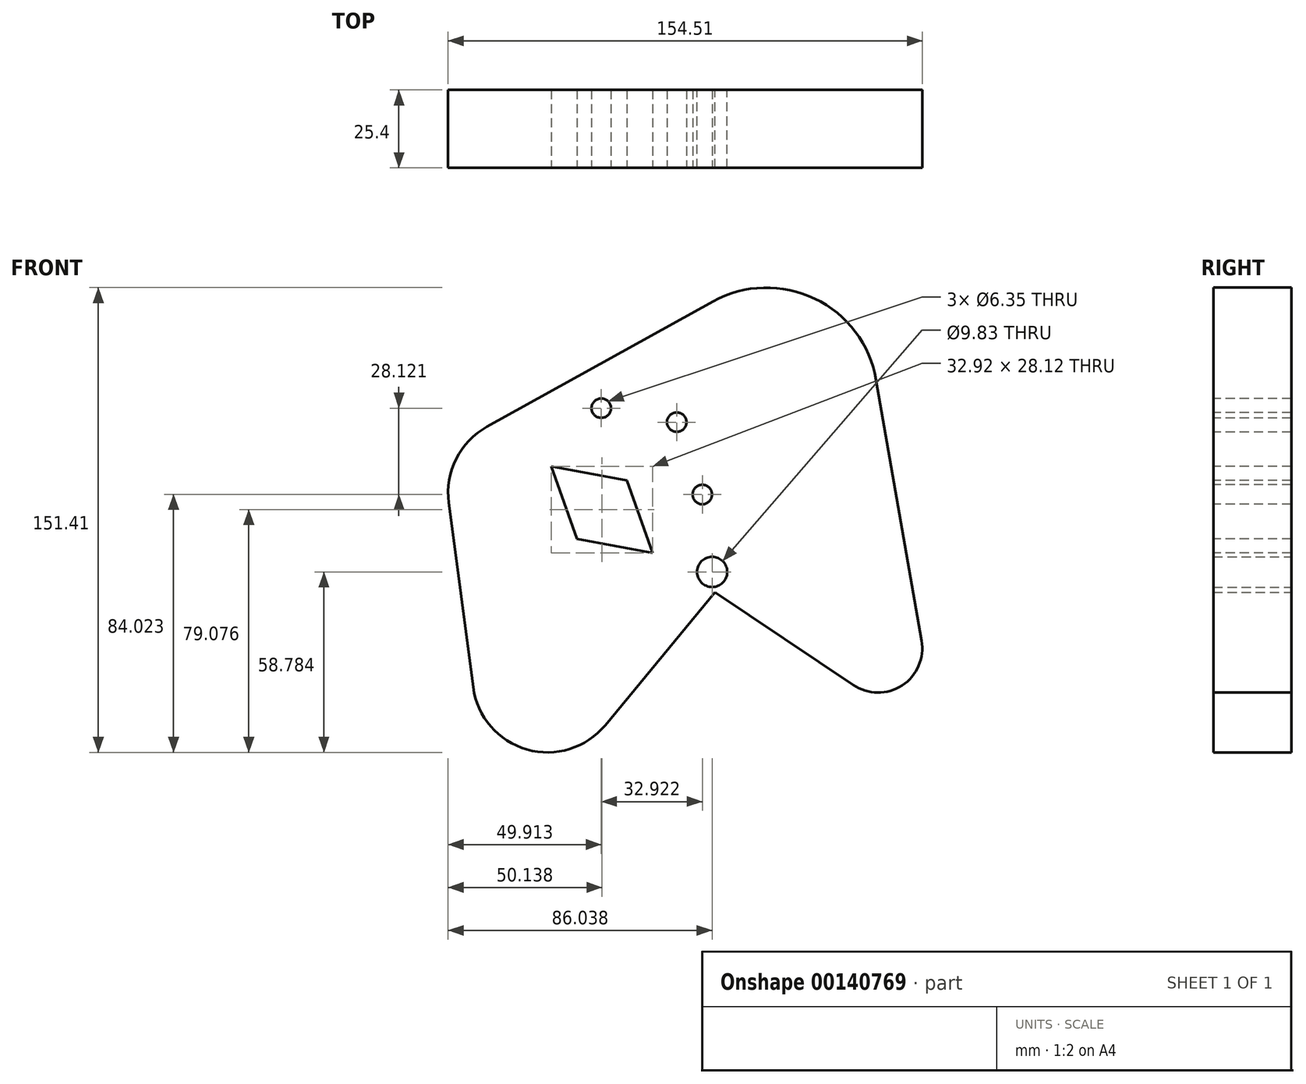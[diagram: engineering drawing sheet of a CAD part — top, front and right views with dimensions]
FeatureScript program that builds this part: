
annotation { "Feature Type Name" : "Feature", "Feature Type Description" : "" }
export const myFeature = defineFeature(function(context is Context, id is Id, definition is map)
    precondition{}
    {
        {
            var Q0;
            Q0=qCreatedBy(makeId("Front.planeOp"),FACE);
            var sketch = newSketch(context, id + "F0", { "sketchPlane" : qUnion([Q0])});
            skCircle(sketch, "E0", {"center": v(-69.46, 62.23) * mm, "radius": 24.64 * mm});
            skCircle(sketch, "E1", {"center": v(-61.73, 2.12) * mm, "radius": 24.43 * mm});
            skCircle(sketch, "E2", {"center": v(-8.07, 36.46) * mm, "radius": 4.92 * mm});
            skCircle(sketch, "E3", {"center": v(9.73, 92.97) * mm, "radius": 36.12 * mm});
            skCircle(sketch, "E4", {"center": v(45.96, 11.61) * mm, "radius": 14.43 * mm});
            skLineSegment(sketch, "E5", {"start": v(-81.4, 83.79) * mm, "end": v(-7.77, 124.57) * mm});
            skLineSegment(sketch, "E6", {"start": v(45.3, 99.33) * mm, "end": v(60.18, 14.1) * mm});
            skLineSegment(sketch, "E7", {"start": v(37.9, -0.37) * mm, "end": v(-10.81, 32.38) * mm});
            skLineSegment(sketch, "E8", {"start": v(-4.28, 33.34) * mm, "end": v(-44.43, -15.3) * mm});
            skLineSegment(sketch, "E9", {"start": v(-93.9, 59) * mm, "end": v(-85.95, -1.08) * mm});
            skSolve(sketch);
        }
        {
            var Q0;
            Q0 = qSketchRegion(id + "F0", true);
            extrude(context, id + "F1", {"entities" : qUnion([Q0]), "depth" : 25.4 * mm});
        }
        {
            var Q0;
            Q0=makeQuery(id+"F1.opExtrude","CAP_FACE",FACE,{"disambiguationData":[OSD([sQuery(id+"F0.wireOp",EDGE,"E0"),sQuery(id+"F0.wireOp",EDGE,"E1"),sQuery(id+"F0.wireOp",EDGE,"E2"),sQuery(id+"F0.wireOp",EDGE,"E3"),sQuery(id+"F0.wireOp",EDGE,"E4"),sQuery(id+"F0.wireOp",EDGE,"E5"),sQuery(id+"F0.wireOp",EDGE,"E6"),sQuery(id+"F0.wireOp",EDGE,"E7"),sQuery(id+"F0.wireOp",EDGE,"E8"),sQuery(id+"F0.wireOp",EDGE,"E9")])],"isStart":false});
            var sketch = newSketch(context, id + "F2", { "sketchPlane" : qUnion([Q0])});
            skCircle(sketch, "E10.cCircle", {"center": v(-35.85, 66.26) * mm, "radius": 25 * mm, "construction": true});
            skLineSegment(sketch, "E10.0", {"start": v(-19.62, 85.27) * mm, "end": v(-11.28, 61.7) * mm});
            skLineSegment(sketch, "E10.1", {"start": v(-11.28, 61.7) * mm, "end": v(-27.51, 42.7) * mm});
            skLineSegment(sketch, "E10.2", {"start": v(-27.51, 42.7) * mm, "end": v(-52.09, 47.25) * mm});
            skLineSegment(sketch, "E10.3", {"start": v(-52.09, 47.25) * mm, "end": v(-60.43, 70.82) * mm});
            skLineSegment(sketch, "E10.4", {"start": v(-60.43, 70.82) * mm, "end": v(-44.2, 89.82) * mm});
            skLineSegment(sketch, "E10.5", {"start": v(-44.2, 89.82) * mm, "end": v(-19.62, 85.27) * mm});
            skLineSegment(sketch, "E11", {"start": v(-60.43, 70.82) * mm, "end": v(-11.28, 61.7) * mm});
            skLineSegment(sketch, "E12", {"start": v(-52.09, 47.25) * mm, "end": v(-19.62, 85.27) * mm});
            skLineSegment(sketch, "E13", {"start": v(-44.2, 89.82) * mm, "end": v(-27.51, 42.7) * mm});
            skSolve(sketch);
        }
        {
            var Q0;
            {var subQ0=sQuery(id+"F2.wireOp",EDGE,"E10.3");Q0=makeQuery(id+"F2.imprint","IMPRINT",FACE,{"disambiguationData":[TD([[makeQuery(id+"F2.imprint","IMPRINT",EDGE,{"derivedFrom":subQ0}),-1.0]])]});}
            extrude(context, id + "F3", {"entities" : qUnion([Q0]), "operationType" : NewBodyOperationType.REMOVE, "oppositeDirection" : true, "depth" : 25.4 * mm});
        }
        {
            var Q0;
            {var subQ0=sQuery(id+"F2.wireOp",EDGE,"E10.2");Q0=makeQuery(id+"F2.imprint","IMPRINT",FACE,{"disambiguationData":[TD([[makeQuery(id+"F2.imprint","IMPRINT",EDGE,{"derivedFrom":subQ0}),-1.0]])]});}
            extrude(context, id + "F4", {"entities" : qUnion([Q0]), "operationType" : NewBodyOperationType.REMOVE, "oppositeDirection" : true, "depth" : 25.4 * mm});
        }
        {
            var Q0;
            Q0=sQuery(id+"F2.wireOp",VERTEX,"E12.end");
            var Q1;
            Q1=makeQuery(id+"F1.opExtrude","SWEPT_BODY",BODY,{"disambiguationData":[OSD([sQuery(id+"F0.wireOp",EDGE,"E0"),sQuery(id+"F0.wireOp",EDGE,"E1"),sQuery(id+"F0.wireOp",EDGE,"E2"),sQuery(id+"F0.wireOp",EDGE,"E3"),sQuery(id+"F0.wireOp",EDGE,"E4"),sQuery(id+"F0.wireOp",EDGE,"E5"),sQuery(id+"F0.wireOp",EDGE,"E6"),sQuery(id+"F0.wireOp",EDGE,"E7"),sQuery(id+"F0.wireOp",EDGE,"E8"),sQuery(id+"F0.wireOp",EDGE,"E9")])]});
            hole(context, id + "F5", {"style" : HoleStyle.SIMPLE, "endStyle" : HoleEndStyle.THROUGH, "holeDiameter" : 6.35 * mm, "locations" : qUnion([Q0]), "scope" : qUnion([Q1]), "isTappedThrough" : true});
        }
        {
            var Q0;
            Q0=sQuery(id+"F2.wireOp",VERTEX,"E13.start");
            var Q1;
            Q1=makeQuery(id+"F1.opExtrude","SWEPT_BODY",BODY,{"disambiguationData":[OSD([sQuery(id+"F0.wireOp",EDGE,"E0"),sQuery(id+"F0.wireOp",EDGE,"E1"),sQuery(id+"F0.wireOp",EDGE,"E2"),sQuery(id+"F0.wireOp",EDGE,"E3"),sQuery(id+"F0.wireOp",EDGE,"E4"),sQuery(id+"F0.wireOp",EDGE,"E5"),sQuery(id+"F0.wireOp",EDGE,"E6"),sQuery(id+"F0.wireOp",EDGE,"E7"),sQuery(id+"F0.wireOp",EDGE,"E8"),sQuery(id+"F0.wireOp",EDGE,"E9")])]});
            hole(context, id + "F6", {"style" : HoleStyle.SIMPLE, "endStyle" : HoleEndStyle.THROUGH, "holeDiameter" : 6.35 * mm, "locations" : qUnion([Q0]), "scope" : qUnion([Q1]), "isTappedThrough" : true});
        }
        {
            var Q0;
            Q0=sQuery(id+"F2.wireOp",VERTEX,"E10.1.start");
            var Q1;
            Q1=makeQuery(id+"F1.opExtrude","SWEPT_BODY",BODY,{"disambiguationData":[OSD([sQuery(id+"F0.wireOp",EDGE,"E0"),sQuery(id+"F0.wireOp",EDGE,"E1"),sQuery(id+"F0.wireOp",EDGE,"E2"),sQuery(id+"F0.wireOp",EDGE,"E3"),sQuery(id+"F0.wireOp",EDGE,"E4"),sQuery(id+"F0.wireOp",EDGE,"E5"),sQuery(id+"F0.wireOp",EDGE,"E6"),sQuery(id+"F0.wireOp",EDGE,"E7"),sQuery(id+"F0.wireOp",EDGE,"E8"),sQuery(id+"F0.wireOp",EDGE,"E9")])]});
            hole(context, id + "F7", {"style" : HoleStyle.SIMPLE, "endStyle" : HoleEndStyle.THROUGH, "holeDiameter" : 6.35 * mm, "locations" : qUnion([Q0]), "scope" : qUnion([Q1]), "isTappedThrough" : true});
        }
    });
